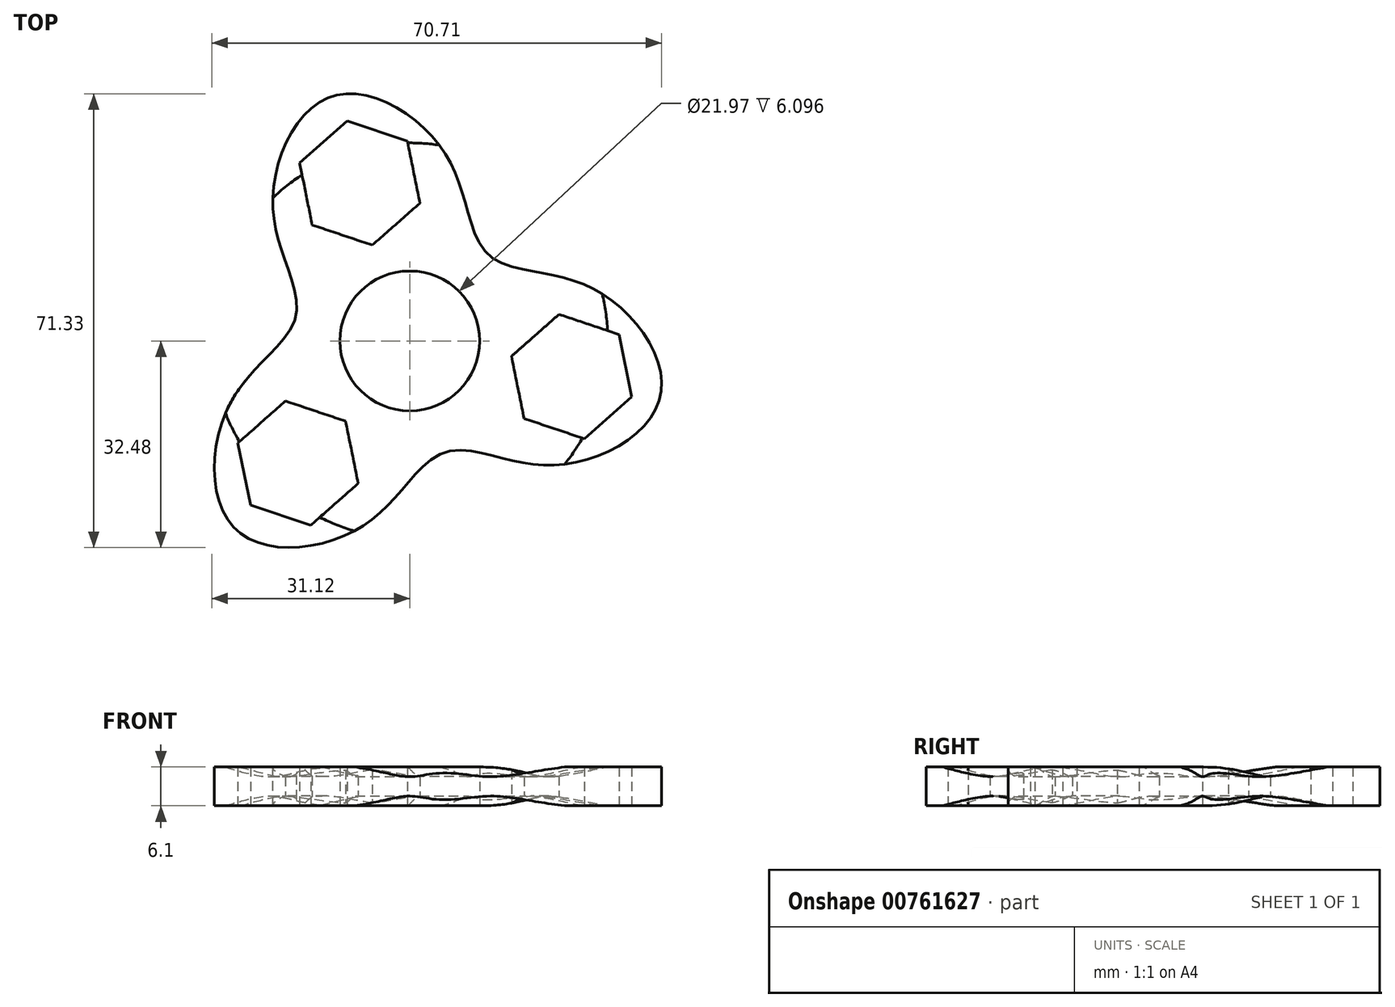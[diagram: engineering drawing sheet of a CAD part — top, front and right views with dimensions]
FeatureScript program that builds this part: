
annotation { "Feature Type Name" : "Feature", "Feature Type Description" : "" }
export const myFeature = defineFeature(function(context is Context, id is Id, definition is map)
    precondition{}
    {
        {
            var Q0;
            Q0=qCreatedBy(makeId("Top.planeOp"),FACE);
            var sketch = newSketch(context, id + "F0", { "sketchPlane" : qUnion([Q0])});
            skCircle(sketch, "E0", {"center": v(0, 0) * mm, "radius": 40.33 * mm, "construction": true});
            skLineSegment(sketch, "E1.0", {"start": v(39.38, -8.67) * mm, "end": v(-27.2, -29.77) * mm, "construction": true});
            skLineSegment(sketch, "E1.1", {"start": v(-27.2, -29.77) * mm, "end": v(-12.18, 38.44) * mm, "construction": true});
            skLineSegment(sketch, "E1.2", {"start": v(-12.18, 38.44) * mm, "end": v(39.38, -8.67) * mm, "construction": true});
            skCircle(sketch, "E2", {"center": v(0, 0) * mm, "radius": 18.33 * mm, "construction": true});
            skLineSegment(sketch, "E3.0", {"start": v(5.54, -17.47) * mm, "end": v(-17.9, 3.94) * mm, "construction": true});
            skLineSegment(sketch, "E3.1", {"start": v(-17.9, 3.94) * mm, "end": v(12.36, 13.53) * mm, "construction": true});
            skLineSegment(sketch, "E3.2", {"start": v(12.36, 13.53) * mm, "end": v(5.54, -17.47) * mm, "construction": true});
            skLineSegment(sketch, "E4", {"start": v(-27.2, -29.77) * mm, "end": v(0, 0) * mm, "construction": true});
            skCircle(sketch, "E5", {"center": v(-27.2, -29.77) * mm, "radius": 14.29 * mm, "construction": true});
            skArc(sketch, "E6", {"start": v(-7.02, -28.86) * mm, "mid": v(-7.93, -8.68) * mm, "end": v(-28.11, -9.59) * mm, "construction": true});
            skLineSegment(sketch, "E7", {"start": v(-17.56, -19.23) * mm, "end": v(-28.11, -9.59) * mm, "construction": true});
            skLineSegment(sketch, "E8", {"start": v(-17.56, -19.23) * mm, "end": v(-7.02, -28.86) * mm, "construction": true});
            skArc(sketch, "E9.1.0", {"start": v(28.5, 8.35) * mm, "mid": v(11.48, -2.53) * mm, "end": v(22.36, -19.55) * mm, "construction": true});
            skLineSegment(sketch, "E9.1.1", {"start": v(25.43, -5.6) * mm, "end": v(22.36, -19.55) * mm, "construction": true});
            skLineSegment(sketch, "E9.1.2", {"start": v(25.43, -5.6) * mm, "end": v(28.5, 8.35) * mm, "construction": true});
            skArc(sketch, "E9.2.0", {"start": v(-21.49, 20.5) * mm, "mid": v(-3.55, 11.2) * mm, "end": v(5.75, 29.14) * mm, "construction": true});
            skLineSegment(sketch, "E9.2.1", {"start": v(-7.87, 24.82) * mm, "end": v(5.75, 29.14) * mm, "construction": true});
            skLineSegment(sketch, "E9.2.2", {"start": v(-7.87, 24.82) * mm, "end": v(-21.49, 20.5) * mm, "construction": true});
            skFitSpline(sketch, "E10", {"points": [v(-28.11, -9.59) * mm, v(-17.9, 3.94) * mm, v(-21.49, 20.5) * mm, v(-12.18, 38.44) * mm, v(5.75, 29.14) * mm, v(12.36, 13.53) * mm, v(28.5, 8.35) * mm, v(39.38, -8.67) * mm, v(22.36, -19.55) * mm, v(5.54, -17.47) * mm, v(-7.02, -28.86) * mm, v(-27.2, -29.77) * mm, v(-28.11, -9.59) * mm]});
            skCircle(sketch, "E11.cCircle", {"center": v(-7.87, 24.82) * mm, "radius": 9.97 * mm, "construction": true});
            skLineSegment(sketch, "E11.0", {"start": v(-0.4, 31.42) * mm, "end": v(1.59, 21.65) * mm});
            skLineSegment(sketch, "E11.1", {"start": v(1.59, 21.65) * mm, "end": v(-5.89, 15.05) * mm});
            skLineSegment(sketch, "E11.2", {"start": v(-5.89, 15.05) * mm, "end": v(-15.34, 18.22) * mm});
            skLineSegment(sketch, "E11.3", {"start": v(-15.34, 18.22) * mm, "end": v(-17.32, 28) * mm});
            skLineSegment(sketch, "E11.4", {"start": v(-17.32, 28) * mm, "end": v(-9.85, 34.6) * mm});
            skLineSegment(sketch, "E11.5", {"start": v(-9.85, 34.6) * mm, "end": v(-0.4, 31.42) * mm});
            skLineSegment(sketch, "E12.1.0", {"start": v(-15.59, -29) * mm, "end": v(-25.04, -25.83) * mm});
            skLineSegment(sketch, "E12.1.1", {"start": v(-8.11, -22.4) * mm, "end": v(-15.59, -29) * mm});
            skLineSegment(sketch, "E12.1.2", {"start": v(-10.09, -12.62) * mm, "end": v(-8.11, -22.4) * mm});
            skLineSegment(sketch, "E12.1.3", {"start": v(-19.54, -9.45) * mm, "end": v(-10.09, -12.62) * mm});
            skLineSegment(sketch, "E12.1.4", {"start": v(-27.02, -16.05) * mm, "end": v(-19.54, -9.45) * mm});
            skLineSegment(sketch, "E12.1.5", {"start": v(-25.04, -25.83) * mm, "end": v(-27.02, -16.05) * mm});
            skLineSegment(sketch, "E12.2.0", {"start": v(32.9, 1) * mm, "end": v(34.88, -8.77) * mm});
            skLineSegment(sketch, "E12.2.1", {"start": v(23.45, 4.18) * mm, "end": v(32.9, 1) * mm});
            skLineSegment(sketch, "E12.2.2", {"start": v(15.98, -2.42) * mm, "end": v(23.45, 4.18) * mm});
            skLineSegment(sketch, "E12.2.3", {"start": v(17.96, -12.2) * mm, "end": v(15.98, -2.42) * mm});
            skLineSegment(sketch, "E12.2.4", {"start": v(27.4, -15.37) * mm, "end": v(17.96, -12.2) * mm});
            skLineSegment(sketch, "E12.2.5", {"start": v(34.88, -8.77) * mm, "end": v(27.4, -15.37) * mm});
            skCircle(sketch, "E13", {"center": v(0, 0) * mm, "radius": 10.99 * mm});
            skSolve(sketch);
        }
        {
            var Q0;
            Q0 = qSketchRegion(id + "F0", true);
            extrude(context, id + "F1", {"entities" : qUnion([Q0]), "depth" : 6.1 * mm, "offsetDistance" : 25.4 * mm});
        }
        {
            var Q0;
            Q0=qCreatedBy(makeId("Front.planeOp"),FACE);
            var sketch = newSketch(context, id + "F2", { "sketchPlane" : qUnion([Q0])});
            skFitSpline(sketch, "E14", {"points": [v(10.99, 6.1) * mm, v(22.06, 4.57) * mm, v(36.53, 6.67) * mm], "startDerivative": vector(38.9, 0.07) * mm, "endDerivative": vector(29.45, 0.06) * mm});
            skLineSegment(sketch, "E15", {"start": v(0, 1.5) * mm, "end": v(0, 4.6) * mm});
            skLineSegment(sketch, "E16", {"start": v(0, 3.05) * mm, "end": v(39.47, 3.05) * mm});
            skFitSpline(sketch, "E17.MirrorCS", {"points": [v(10.99, 0) * mm, v(22.06, 1.52) * mm, v(36.53, -0.57) * mm], "startDerivative": vector(38.9, -0.07) * mm, "endDerivative": vector(29.45, -0.06) * mm});
            skLineSegment(sketch, "E18", {"start": v(22.06, 4.57) * mm, "end": v(22.06, 6.1) * mm, "construction": true});
            skLineSegment(sketch, "E19.top", {"start": v(10.99, 9.04) * mm, "end": v(36.53, 9.04) * mm});
            skLineSegment(sketch, "E19.left", {"start": v(10.99, 6.1) * mm, "end": v(10.99, 9.04) * mm});
            skLineSegment(sketch, "E20.MirrorCS", {"start": v(10.99, -2.94) * mm, "end": v(36.53, -2.94) * mm});
            skLineSegment(sketch, "E21.MirrorCS", {"start": v(10.99, 0) * mm, "end": v(10.99, -2.94) * mm});
            skPoint(sketch, "E19.right.start.orphan", {"position": v(36.53, 6.57) * mm});
            skPoint(sketch, "E22.MirrorCS.end.orphan", {"position": v(36.53, -2.94) * mm});
            skPoint(sketch, "E22.MirrorCS.start.orphan", {"position": v(36.53, -0.47) * mm});
            skLineSegment(sketch, "E23", {"start": v(36.53, -0.57) * mm, "end": v(36.53, -2.94) * mm});
            skLineSegment(sketch, "E24", {"start": v(36.53, 9.04) * mm, "end": v(36.53, 6.67) * mm});
            skLineSegment(sketch, "E25.0", {"start": v(10.99, 1.5) * mm, "end": v(10.99, 4.6) * mm});
            skSolve(sketch);
        }
        {
            var Q0;
            Q0=makeQuery(id+"F2.imprint","IMPRINT",FACE,{"disambiguationData":[TD([[makeQuery(id+"F2.imprint","IMPRINT",EDGE,{"derivedFrom":sQuery(id+"F2.wireOp",EDGE,"E14")}),1.0]])]});
            var Q1;
            Q1=sQuery(id+"F2.wireOp",EDGE,"E15");
            revolve(context, id + "F3", {"operationType" : NewBodyOperationType.REMOVE, "surfaceOperationType" : NewSurfaceOperationType.NEW, "entities" : qUnion([Q0]), "axis" : qUnion([Q1]), "revolveType" : RevolveType.FULL, "oppositeDirection" : true});
        }
        {
            var Q0;
            Q0=makeQuery(id+"F2.imprint","IMPRINT",FACE,{"disambiguationData":[TD([[makeQuery(id+"F2.imprint","IMPRINT",EDGE,{"derivedFrom":sQuery(id+"F2.wireOp",EDGE,"E17.MirrorCS")}),-1.0]])]});
            var Q1;
            Q1=sQuery(id+"F2.wireOp",EDGE,"E15");
            revolve(context, id + "F4", {"operationType" : NewBodyOperationType.REMOVE, "surfaceOperationType" : NewSurfaceOperationType.NEW, "entities" : qUnion([Q0]), "axis" : qUnion([Q1]), "revolveType" : RevolveType.FULL, "oppositeDirection" : true});
        }
    });
